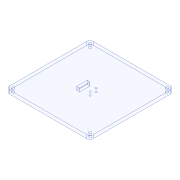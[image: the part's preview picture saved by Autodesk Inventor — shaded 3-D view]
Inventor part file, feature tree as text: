
AUTODESK INVENTOR PART (.ipt)
format: ipt  version: 2020 (Build 240168000, 168)  size: 127,488 bytes
history: native  units: mm
features: sketch x4, extrude x3, fillet x1
ambient origin geometry x8: Origin, YZ Plane, XZ Plane, XY Plane, X Axis, Y Axis, Z Axis, Center Point
bodies: Solid1 (feature_tree)
feature tree (8):
  extrude  "Extrusion1"  Depth=120.0mm
  extrude  "Extrusion2"  Depth=5.0mm
  fillet  "Fillet1"  Radius=110.0mm
  sketch  "Sketch3"  dims[d6=4.0mm d7=4.0mm]
  extrude  "Extrusion3"  Depth=4.0mm
  sketch  "Sketch1"  dims[d0=120.0mm d1=120.0mm]
  sketch  "Sketch2"  dims[d2=5.0mm d3=0.0mm d4=110.0mm d5=110.0mm]
  sketch  "Sketch4"  dims[d8=4.0mm d9=4.0mm d10=5.0mm d11=0.0mm d12=5.0mm d13=15.0mm d14=4.0mm d15=15.0mm d16=9.5mm d17=14.0mm d18=14.0mm d19=2.5mm d20=2.5mm d21=8.5mm d22=4.25mm d23=10.0mm d24=0.0mm]
